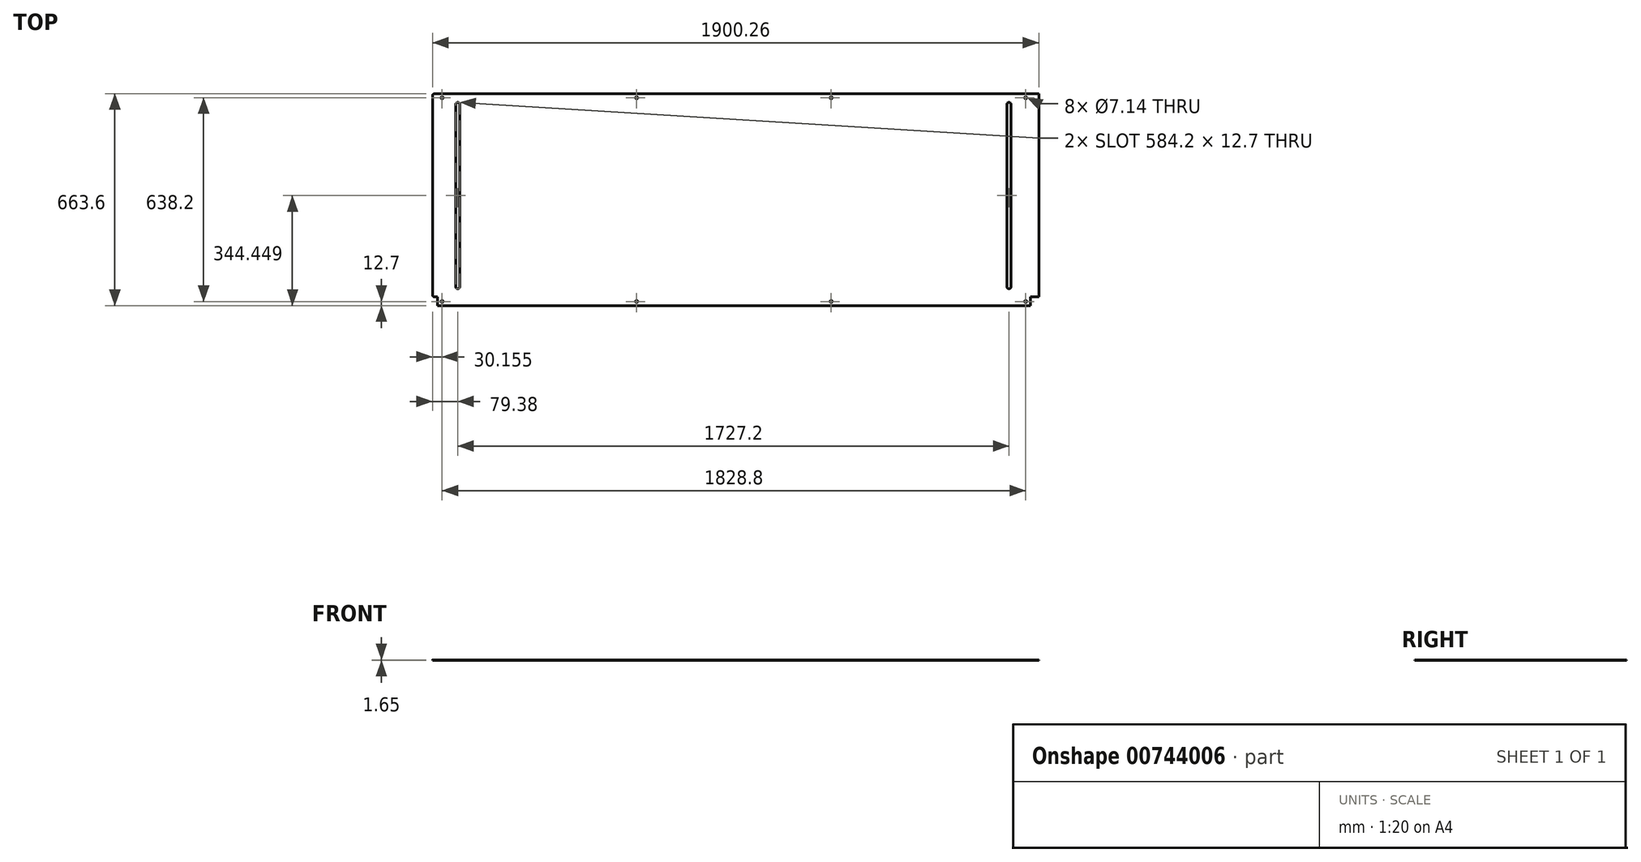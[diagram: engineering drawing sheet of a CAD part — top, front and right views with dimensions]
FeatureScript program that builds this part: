
annotation { "Feature Type Name" : "Feature", "Feature Type Description" : "" }
export const myFeature = defineFeature(function(context is Context, id is Id, definition is map)
    precondition{}
    {
        {
            var Q0;
            Q0=qCreatedBy(makeId("Top.planeOp"),FACE);
            var sketch = newSketch(context, id + "F0", { "sketchPlane" : qUnion([Q0])});
            skLineSegment(sketch, "E0.bottom", {"start": v(0, 0) * mm, "end": v(1857.38, 0) * mm});
            skLineSegment(sketch, "E0.top", {"start": v(0, -636.6) * mm, "end": v(1857.38, -636.6) * mm});
            skLineSegment(sketch, "E0.left", {"start": v(0, 0) * mm, "end": v(0, -636.6) * mm});
            skLineSegment(sketch, "E0.right", {"start": v(1857.38, 0) * mm, "end": v(1857.38, -636.6) * mm});
            skLineSegment(sketch, "E1.top", {"start": v(0, -663.6) * mm, "end": v(1857.38, -663.6) * mm});
            skLineSegment(sketch, "E1.left", {"start": v(0, -636.6) * mm, "end": v(0, -663.6) * mm});
            skLineSegment(sketch, "E1.right", {"start": v(1857.38, -636.6) * mm, "end": v(1857.38, -663.6) * mm});
            skLineSegment(sketch, "E2.bottom", {"start": v(1857.38, 0) * mm, "end": v(1884.38, 0) * mm});
            skLineSegment(sketch, "E2.top", {"start": v(1857.38, -636.6) * mm, "end": v(1884.38, -636.6) * mm});
            skLineSegment(sketch, "E2.right", {"start": v(1884.38, 0) * mm, "end": v(1884.38, -636.6) * mm});
            skLineSegment(sketch, "E3.bottom", {"start": v(0, 0) * mm, "end": v(-9.52, 0) * mm});
            skLineSegment(sketch, "E3.top", {"start": v(0, -636.6) * mm, "end": v(-9.52, -636.6) * mm});
            skLineSegment(sketch, "E3.right", {"start": v(-15.87, -6.35) * mm, "end": v(-15.87, -630.25) * mm});
            skPoint(sketch, "E4.visualSharp", {"position": v(-15.87, -636.6) * mm});
            skArc(sketch, "E4.filletArc", {"start": v(-15.87, -630.25) * mm, "mid": v(-14.02, -634.74) * mm, "end": v(-9.52, -636.6) * mm});
            skPoint(sketch, "E5.visualSharp", {"position": v(-15.87, 0) * mm});
            skArc(sketch, "E5.filletArc", {"start": v(-9.52, 0) * mm, "mid": v(-14.02, -1.86) * mm, "end": v(-15.87, -6.35) * mm});
            skCircle(sketch, "E6", {"center": v(1843.07, -12.7) * mm, "radius": 3.57 * mm});
            skCircle(sketch, "E7.1.0.0", {"center": v(1233.47, -12.7) * mm, "radius": 3.57 * mm});
            skCircle(sketch, "E7.2.0.0", {"center": v(623.87, -12.7) * mm, "radius": 3.57 * mm});
            skCircle(sketch, "E7.3.0.0", {"center": v(14.27, -12.7) * mm, "radius": 3.57 * mm});
            skLineSegment(sketch, "E7.direction1", {"start": v(1843.07, -12.7) * mm, "end": v(1233.47, -12.7) * mm, "construction": true});
            skCircle(sketch, "E8", {"center": v(1843.07, -650.9) * mm, "radius": 3.57 * mm});
            skCircle(sketch, "E9.1.0.0", {"center": v(1233.47, -650.9) * mm, "radius": 3.57 * mm});
            skCircle(sketch, "E9.2.0.0", {"center": v(623.87, -650.9) * mm, "radius": 3.57 * mm});
            skCircle(sketch, "E9.3.0.0", {"center": v(14.27, -650.9) * mm, "radius": 3.57 * mm});
            skLineSegment(sketch, "E9.direction1", {"start": v(1843.07, -650.9) * mm, "end": v(1233.47, -650.9) * mm, "construction": true});
            skCircle(sketch, "E10", {"center": v(63.5, -33.4) * mm, "radius": 6.35 * mm});
            skCircle(sketch, "E11.0.1.0", {"center": v(63.5, -604.9) * mm, "radius": 6.35 * mm});
            skCircle(sketch, "E11.1.0.0", {"center": v(1790.7, -33.4) * mm, "radius": 6.35 * mm});
            skCircle(sketch, "E11.1.1.0", {"center": v(1790.7, -604.9) * mm, "radius": 6.35 * mm});
            skLineSegment(sketch, "E11.direction1", {"start": v(63.5, -33.4) * mm, "end": v(1790.7, -33.4) * mm, "construction": true});
            skLineSegment(sketch, "E11.direction2", {"start": v(63.5, -33.4) * mm, "end": v(63.5, -604.9) * mm, "construction": true});
            skLineSegment(sketch, "E12", {"start": v(1797.05, -33.4) * mm, "end": v(1797.05, -604.9) * mm});
            skLineSegment(sketch, "E13", {"start": v(1784.35, -604.9) * mm, "end": v(1784.35, -33.4) * mm});
            skLineSegment(sketch, "E14", {"start": v(69.85, -33.4) * mm, "end": v(69.85, -604.9) * mm});
            skLineSegment(sketch, "E15", {"start": v(57.15, -604.9) * mm, "end": v(57.15, -33.4) * mm});
            skSolve(sketch);
        }
        {
            var Q0;
            Q0=makeQuery(id+"F0.imprint","IMPRINT",FACE,{"disambiguationData":[TD([[makeQuery(id+"F0.imprint","IMPRINT",EDGE,{"derivedFrom":sQuery(id+"F0.wireOp",EDGE,"E3.bottom")}),1.0]])]});
            var Q1;
            Q1=makeQuery(id+"F0.imprint","IMPRINT",FACE,{"disambiguationData":[TD([[makeQuery(id+"F0.imprint","IMPRINT",EDGE,{"derivedFrom":sQuery(id+"F0.wireOp",EDGE,"E0.bottom")}),-1.0]])]});
            var Q2;
            Q2=makeQuery(id+"F0.imprint","IMPRINT",FACE,{"disambiguationData":[TD([[makeQuery(id+"F0.imprint","IMPRINT",EDGE,{"derivedFrom":sQuery(id+"F0.wireOp",EDGE,"E0.top")}),-1.0]])]});
            var Q3;
            Q3=makeQuery(id+"F0.imprint","IMPRINT",FACE,{"disambiguationData":[TD([[makeQuery(id+"F0.imprint","IMPRINT",EDGE,{"derivedFrom":sQuery(id+"F0.wireOp",EDGE,"E2.bottom")}),-1.0]])]});
            extrude(context, id + "F1", {"entities" : qUnion([Q0, Q1, Q2, Q3]), "depth" : 1.65 * mm, "offsetDistance" : 25.4 * mm});
        }
    });
